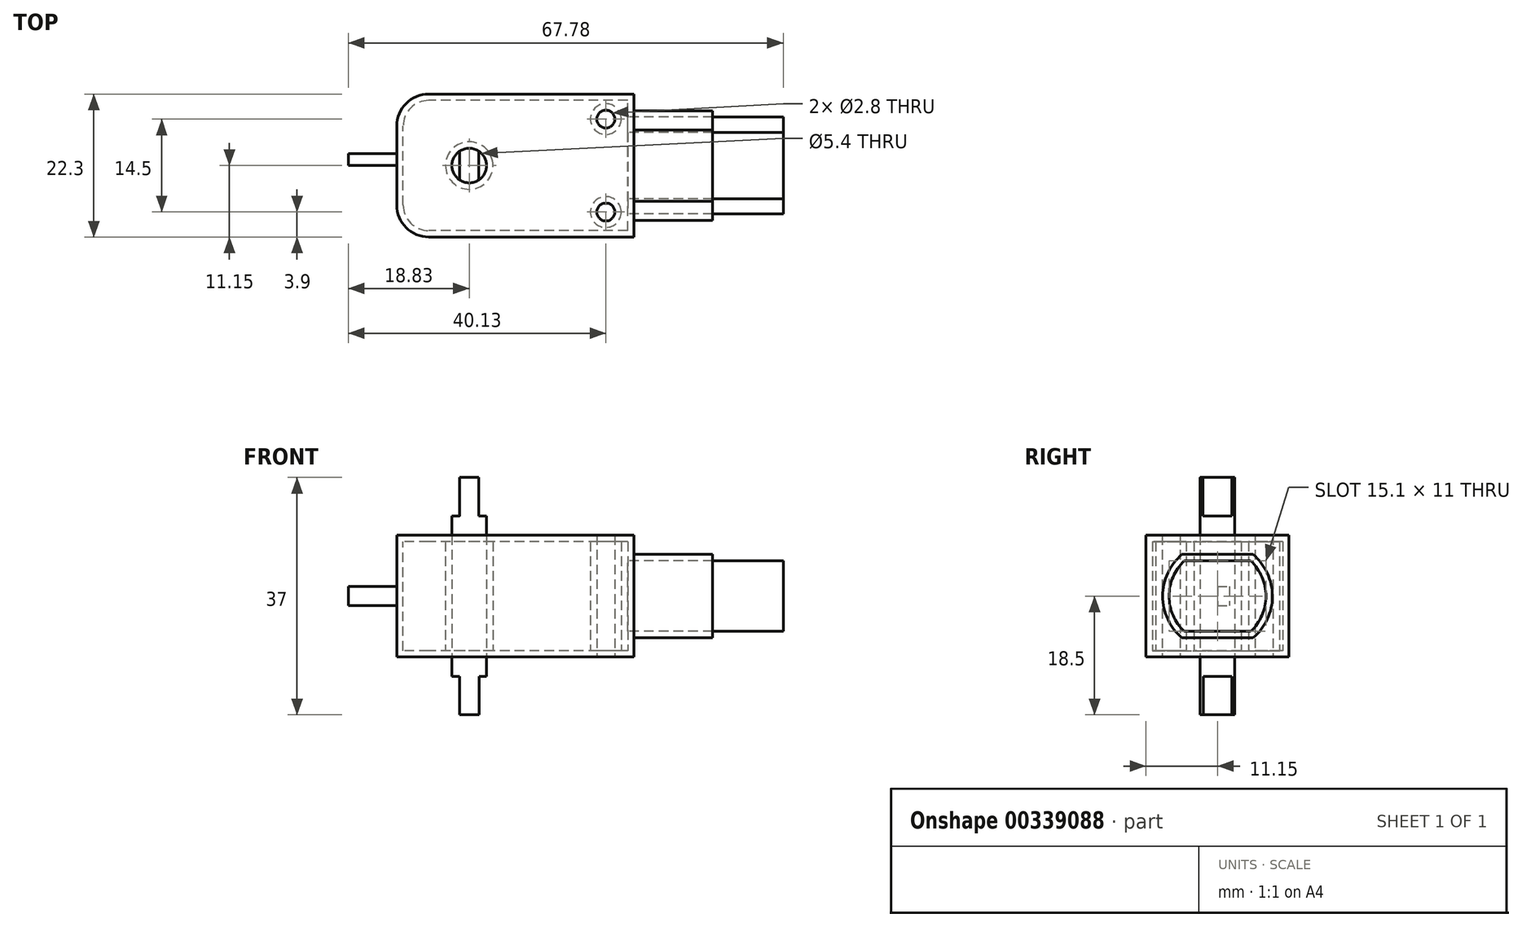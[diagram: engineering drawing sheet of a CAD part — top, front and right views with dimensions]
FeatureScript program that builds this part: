
annotation { "Feature Type Name" : "Feature", "Feature Type Description" : "" }
export const myFeature = defineFeature(function(context is Context, id is Id, definition is map)
    precondition{}
    {
        {
            var Q0;
            Q0=qCreatedBy(makeId("Top.planeOp"),FACE);
            var sketch = newSketch(context, id + "F0", { "sketchPlane" : qUnion([Q0])});
            skLineSegment(sketch, "E0.bottom", {"start": v(18.5, -11.15) * mm, "end": v(-13.5, -11.15) * mm});
            skLineSegment(sketch, "E0.top", {"start": v(18.5, 11.15) * mm, "end": v(-13.5, 11.15) * mm});
            skLineSegment(sketch, "E0.left", {"start": v(18.5, -11.15) * mm, "end": v(18.5, 11.15) * mm});
            skLineSegment(sketch, "E0.right", {"start": v(-18.5, -6.15) * mm, "end": v(-18.5, 6.15) * mm});
            skPoint(sketch, "E0.middle", {"position": v(0, 0) * mm});
            skLineSegment(sketch, "E1", {"start": v(21.81, 11.15) * mm, "end": v(21.81, -11.15) * mm});
            skCircle(sketch, "E2", {"center": v(14.1, 7.25) * mm, "radius": 1.4 * mm});
            skCircle(sketch, "E3", {"center": v(14.1, -7.25) * mm, "radius": 1.4 * mm});
            skCircle(sketch, "E4", {"center": v(-7.2, 0) * mm, "radius": 2.7 * mm});
            skLineSegment(sketch, "E5", {"start": v(-18.5, 1.88) * mm, "end": v(-26.03, 1.88) * mm});
            skLineSegment(sketch, "E6", {"start": v(-26.03, 1.88) * mm, "end": v(-26.03, 0) * mm});
            skLineSegment(sketch, "E7", {"start": v(-26.03, 0) * mm, "end": v(-18.5, 0) * mm});
            skPoint(sketch, "E8.visualSharp", {"position": v(-18.5, 11.15) * mm});
            skArc(sketch, "E8.filletArc", {"start": v(-13.5, 11.15) * mm, "mid": v(-17.04, 9.69) * mm, "end": v(-18.5, 6.15) * mm});
            skPoint(sketch, "E9.visualSharp", {"position": v(-18.5, -11.15) * mm});
            skArc(sketch, "E9.filletArc", {"start": v(-18.5, -6.15) * mm, "mid": v(-17.04, -9.69) * mm, "end": v(-13.5, -11.15) * mm});
            skSolve(sketch);
        }
        {
            var Q0;
            {var subQ0=sQuery(id+"F0.wireOp",EDGE,"E0.left");Q0=makeQuery(id+"F0.imprint","IMPRINT",FACE,{"disambiguationData":[TD([[makeQuery(id+"F0.imprint","IMPRINT",EDGE,{"derivedFrom":subQ0}),1.0]])]});}
            var Q1;
            {var subQ1=sQuery(id+"F0.wireOp",EDGE,"E1");Q1=makeQuery(id+"F0.imprint","IMPRINT",FACE,{"disambiguationData":[TD([[makeQuery(id+"F0.imprint","IMPRINT",EDGE,{"derivedFrom":subQ1}),-1.0]])]});}
            extrude(context, id + "F1", {"entities" : qUnion([Q0, Q1]), "depth" : 19 * mm, "offsetDistance" : 25 * mm, "symmetric" : true});
        }
        {
            var Q0;
            {var subQ0=sQuery(id+"F0.wireOp",EDGE,"E5");Q0=makeQuery(id+"F0.imprint","IMPRINT",FACE,{"disambiguationData":[TD([[makeQuery(id+"F0.imprint","IMPRINT",EDGE,{"derivedFrom":subQ0}),1.0]])]});}
            extrude(context, id + "F2", {"entities" : qUnion([Q0]), "operationType" : NewBodyOperationType.ADD, "depth" : 3 * mm, "symmetric" : true});
        }
        {
            var Q0;
            Q0=makeQuery(id+"F0.imprint","IMPRINT",FACE,{"disambiguationData":[TD([[makeQuery(id+"F0.imprint","IMPRINT",EDGE,{"derivedFrom":sQuery(id+"F0.wireOp",EDGE,"E4")}),1.0]])]});
            extrude(context, id + "F3", {"entities" : qUnion([Q0]), "depth" : 37 * mm, "symmetric" : true});
        }
        {
            var Q0;
            Q0=makeQuery(id+"F1.opExtrude","SWEPT_FACE",FACE,{"disambiguationData":[OSD([sQuery(id+"F0.wireOp",EDGE,"E0.left")])]});
            var sketch = newSketch(context, id + "F4", { "sketchPlane" : qUnion([Q0])});
            skArc(sketch, "E10", {"start": v(-5.55, 6.5) * mm, "mid": v(-8.55, 0) * mm, "end": v(-5.55, -6.5) * mm});
            skLineSegment(sketch, "E11.bottom", {"start": v(5.55, -6.5) * mm, "end": v(-5.55, -6.5) * mm});
            skLineSegment(sketch, "E11.top", {"start": v(5.55, 6.5) * mm, "end": v(-5.55, 6.5) * mm});
            skPoint(sketch, "E11.left.end.orphan", {"position": v(10.32, 6.5) * mm});
            skPoint(sketch, "E12.orphan", {"position": v(11.23, -6.5) * mm});
            skPoint(sketch, "E11.right.start.orphan", {"position": v(-10.32, -6.5) * mm});
            skPoint(sketch, "E13.orphan", {"position": v(-11.23, 6.5) * mm});
            skArc(sketch, "E14.trimOffspring", {"start": v(5.55, -6.5) * mm, "mid": v(8.55, 0) * mm, "end": v(5.55, 6.5) * mm});
            skSolve(sketch);
        }
        {
            var Q0;
            Q0=makeQuery(id+"F4.imprint","IMPRINT",FACE,{"disambiguationData":[TD([[makeQuery(id+"F4.imprint","IMPRINT",EDGE,{"derivedFrom":sQuery(id+"F4.wireOp",EDGE,"E10")}),1.0]])]});
            extrude(context, id + "F5", {"entities" : qUnion([Q0]), "operationType" : NewBodyOperationType.ADD, "depth" : 12.25 * mm, "offsetDistance" : 25 * mm});
        }
        {
            var Q0;
            Q0=makeQuery(id+"F5.opExtrude","CAP_FACE",FACE,{"disambiguationData":[OSD([sQuery(id+"F4.wireOp",EDGE,"E10"),sQuery(id+"F4.wireOp",EDGE,"E11.bottom"),sQuery(id+"F4.wireOp",EDGE,"E11.top"),sQuery(id+"F4.wireOp",EDGE,"E14.trimOffspring")])],"isStart":false});
            shell(context, id + "F6", {"entities" : qUnion([Q0]), "thickness" : 1 * mm});
        }
        {
            var Q0;
            Q0=makeQuery(id+"F5.opExtrude","CAP_FACE",FACE,{"disambiguationData":[OSD([sQuery(id+"F4.wireOp",EDGE,"E10"),sQuery(id+"F4.wireOp",EDGE,"E11.bottom"),sQuery(id+"F4.wireOp",EDGE,"E11.top"),sQuery(id+"F4.wireOp",EDGE,"E14.trimOffspring")])],"isStart":false});
            var sketch = newSketch(context, id + "F7", { "sketchPlane" : qUnion([Q0])});
            skArc(sketch, "E15.0", {"start": v(-5.17, 5.5) * mm, "mid": v(-7.55, 0) * mm, "end": v(-5.17, -5.5) * mm});
            skLineSegment(sketch, "E15.1", {"start": v(5.17, 5.5) * mm, "end": v(-5.17, 5.5) * mm});
            skArc(sketch, "E15.2", {"start": v(5.17, -5.5) * mm, "mid": v(7.55, 0) * mm, "end": v(5.17, 5.5) * mm});
            skLineSegment(sketch, "E15.3", {"start": v(5.17, -5.5) * mm, "end": v(-5.17, -5.5) * mm});
            skSolve(sketch);
        }
        {
            var Q0;
            Q0=makeQuery(id+"F3.opExtrude","CAP_FACE",FACE,{"disambiguationData":[OSD([sQuery(id+"F0.wireOp",EDGE,"E4")])],"isStart":false});
            var sketch = newSketch(context, id + "F8", { "sketchPlane" : qUnion([Q0])});
            skLineSegment(sketch, "E16.bottom", {"start": v(-5.71, -2.25) * mm, "end": v(-8.69, -2.25) * mm});
            skLineSegment(sketch, "E16.top", {"start": v(-5.71, 2.25) * mm, "end": v(-8.69, 2.25) * mm});
            skLineSegment(sketch, "E16.left", {"start": v(-5.71, -2.25) * mm, "end": v(-5.71, 2.25) * mm});
            skLineSegment(sketch, "E16.right", {"start": v(-8.69, -2.25) * mm, "end": v(-8.69, 2.25) * mm});
            skPoint(sketch, "E16.middle", {"position": v(-7.2, 0) * mm});
            skSolve(sketch);
        }
        {
            var Q0;
            {var subQ0=sQuery(id+"F8.wireOp",EDGE,"E16.right");Q0=makeQuery(id+"F8.imprint","IMPRINT",FACE,{"disambiguationData":[TD([[makeQuery(id+"F8.imprint","IMPRINT",EDGE,{"derivedFrom":subQ0}),1.0]])]});}
            var Q1;
            {var subQ0=sQuery(id+"F8.wireOp",EDGE,"E16.left");Q1=makeQuery(id+"F8.imprint","IMPRINT",FACE,{"disambiguationData":[TD([[makeQuery(id+"F8.imprint","IMPRINT",EDGE,{"derivedFrom":subQ0}),-1.0]])]});}
            extrude(context, id + "F9", {"entities" : qUnion([Q0, Q1]), "operationType" : NewBodyOperationType.REMOVE, "oppositeDirection" : true, "depth" : 6 * mm});
        }
        {
            var Q0;
            Q0=makeQuery(id+"F3.opExtrude","CAP_FACE",FACE,{"disambiguationData":[OSD([sQuery(id+"F0.wireOp",EDGE,"E4")])],"isStart":true});
            var sketch = newSketch(context, id + "F10", { "sketchPlane" : qUnion([Q0])});
            skLineSegment(sketch, "E17.bottom", {"start": v(-5.67, 2.23) * mm, "end": v(-8.73, 2.23) * mm});
            skLineSegment(sketch, "E17.top", {"start": v(-5.67, -2.23) * mm, "end": v(-8.73, -2.23) * mm});
            skLineSegment(sketch, "E17.left", {"start": v(-5.67, 2.23) * mm, "end": v(-5.67, -2.23) * mm});
            skLineSegment(sketch, "E17.right", {"start": v(-8.73, 2.23) * mm, "end": v(-8.73, -2.23) * mm});
            skPoint(sketch, "E17.middle", {"position": v(-7.2, 0) * mm});
            skSolve(sketch);
        }
        {
            var Q0;
            {var subQ0=sQuery(id+"F10.wireOp",EDGE,"E17.right");Q0=makeQuery(id+"F10.imprint","IMPRINT",FACE,{"disambiguationData":[TD([[makeQuery(id+"F10.imprint","IMPRINT",EDGE,{"derivedFrom":subQ0}),-1.0]])]});}
            var Q1;
            {var subQ0=sQuery(id+"F10.wireOp",EDGE,"E17.left");Q1=makeQuery(id+"F10.imprint","IMPRINT",FACE,{"disambiguationData":[TD([[makeQuery(id+"F10.imprint","IMPRINT",EDGE,{"derivedFrom":subQ0}),1.0]])]});}
            extrude(context, id + "F11", {"entities" : qUnion([Q0, Q1]), "operationType" : NewBodyOperationType.REMOVE, "oppositeDirection" : true, "depth" : 6 * mm});
        }
        {
            var Q0;
            Q0=makeQuery(id+"F7.imprint","IMPRINT",FACE,{"disambiguationData":[TD([[makeQuery(id+"F7.imprint","IMPRINT",EDGE,{"derivedFrom":sQuery(id+"F7.wireOp",EDGE,"E15.0")}),1.0]])]});
            extrude(context, id + "F12", {"entities" : qUnion([Q0]), "depth" : 11 * mm, "offsetDistance" : 25 * mm});
        }
    });
